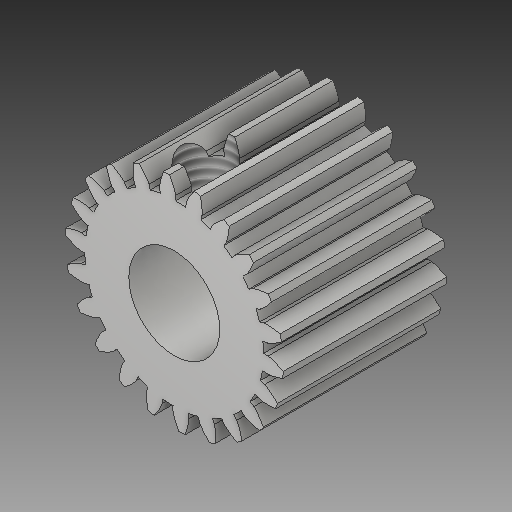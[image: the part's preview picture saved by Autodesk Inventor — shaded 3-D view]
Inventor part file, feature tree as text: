
AUTODESK INVENTOR PART (.ipt)
format: ipt  version: 2018 (Build 220112000, 112)  size: 613,888 bytes
history: native  units: in
note: dims shown in document units (in); Inventor stores cm internally (conversion verified against a paired STEP export)
features: sketch x6, extrude x5, other x2, plane x2, pattern_circular x1, thread x1
ambient origin geometry x8: Origin, YZ Plane, XZ Plane, XY Plane, X Axis, Y Axis, Z Axis, Center Point
bodies: Solid1 (feature_tree)
feature tree (17):
  sketch  "Sketch2"  dims[d0=0.4331in d1=0.1374in]
  extrude  "Extrusion1"  Depth=0.1374in
  extrude  "Extrusion3"  Depth=0.0394in
  pattern_circular  "Circular Pattern1"  [2 undecoded]
  extrude  "Extrusion12"  Depth=0.3937in TaperAngle=360.0deg
  extrude  "Extrusion19"  Depth=0.3937in
  other  "Work Point1"
  plane  "Work Plane16"
  extrude  "Extrusion20"  Depth=0.3937in
  thread  "Thread1"  [1 undecoded]
  plane  "Work Plane17"
  sketch  "Sketch4"  dims[d6=0.0741in d7=0.0394in]
  sketch  "Sketch5"  dims[d8=0.0347in]
  sketch  "Sketch24"  dims[d9=0.0281in]
  sketch  "Sketch47"  dims[d10=0.5906in]
  other  "Work Axis5"
  sketch  "Sketch48"  dims[d12=0.3543in d13=0.0in d16=0.1969in d17=0.0in d18=8.6614in d19=360.0deg d61=0.0472in d62=0.1213in d64=0.0098in d121=0.4724in d122=0.9449in d123=0.3937in d124=0.0in d183=0.1969in d184=0.3937in d185=0.0in d186=0.1102in d188=0.3937in d189=0.0in d190=0.3937in d191=0.0in d192=0.0866in]
note: 3 required parameter values undecoded (feature->parameter linkage not recoverable at this tier; creation-order binding heuristic only, values carry confidence <= 0.55)
